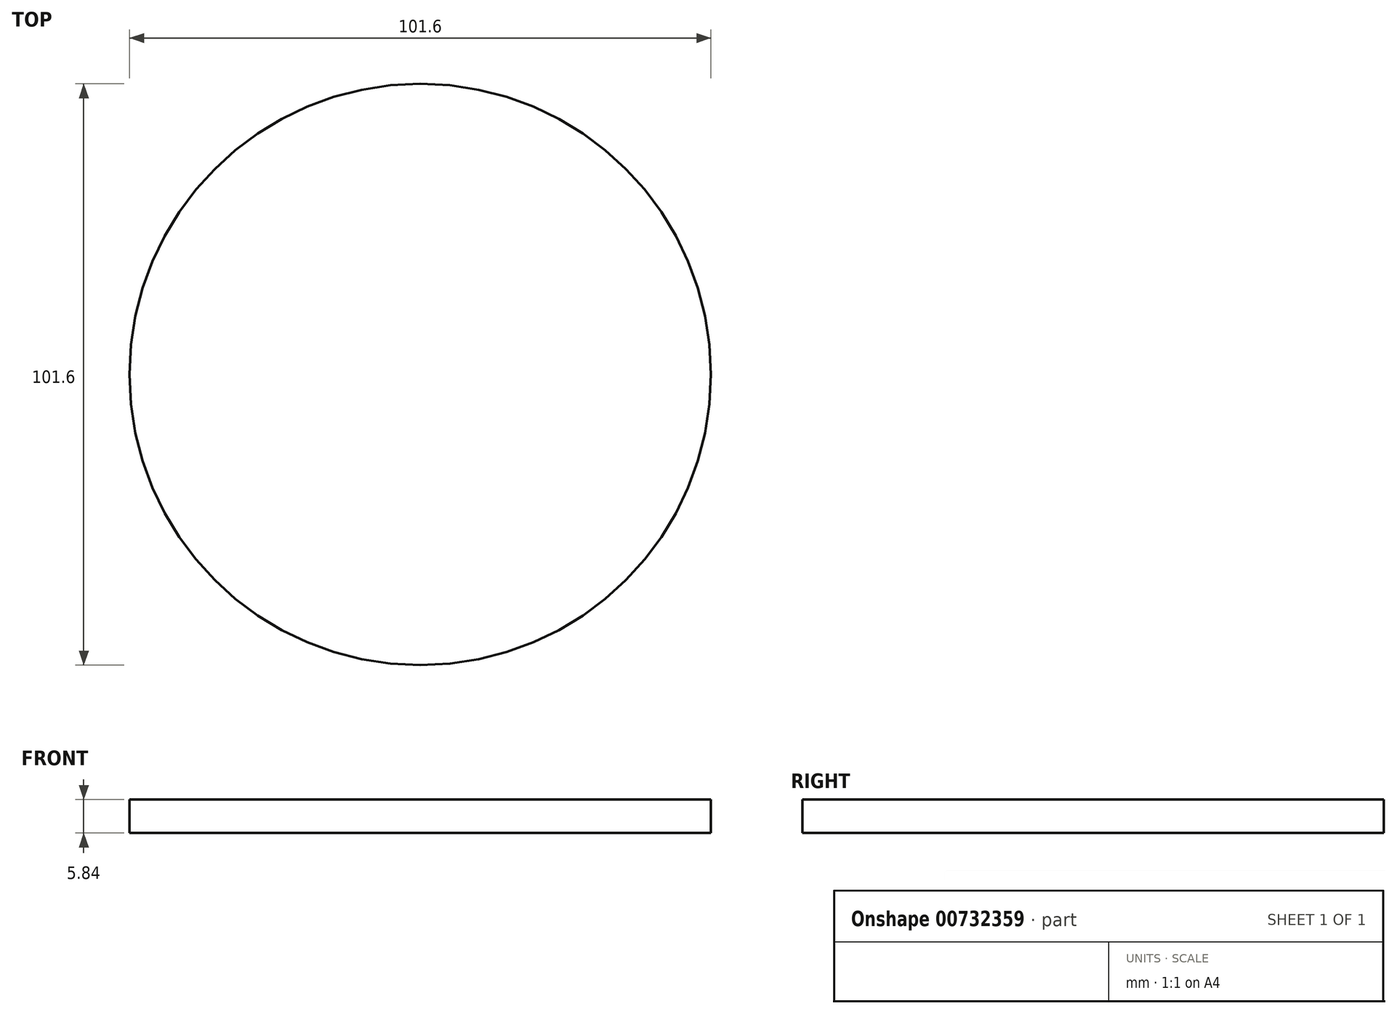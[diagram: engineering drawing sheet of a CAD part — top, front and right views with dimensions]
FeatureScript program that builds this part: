
annotation { "Feature Type Name" : "Feature", "Feature Type Description" : "" }
export const myFeature = defineFeature(function(context is Context, id is Id, definition is map)
    precondition{}
    {
        {
            var Q0;
            Q0=qCreatedBy(makeId("Top.planeOp"),FACE);
            var sketch = newSketch(context, id + "F0", { "sketchPlane" : qUnion([Q0])});
            skCircle(sketch, "E0", {"center": v(0, 0) * mm, "radius": 50.8 * mm});
            skSolve(sketch);
        }
        {
            var Q0;
            Q0=makeQuery(id+"F0.imprint","IMPRINT",FACE,{"disambiguationData":[TD([[makeQuery(id+"F0.imprint","IMPRINT",EDGE,{"derivedFrom":sQuery(id+"F0.wireOp",EDGE,"E0")}),1.0]])]});
            extrude(context, id + "F1", {"entities" : qUnion([Q0]), "depth" : 5.84 * mm, "offsetDistance" : 25.4 * mm});
        }
    });
